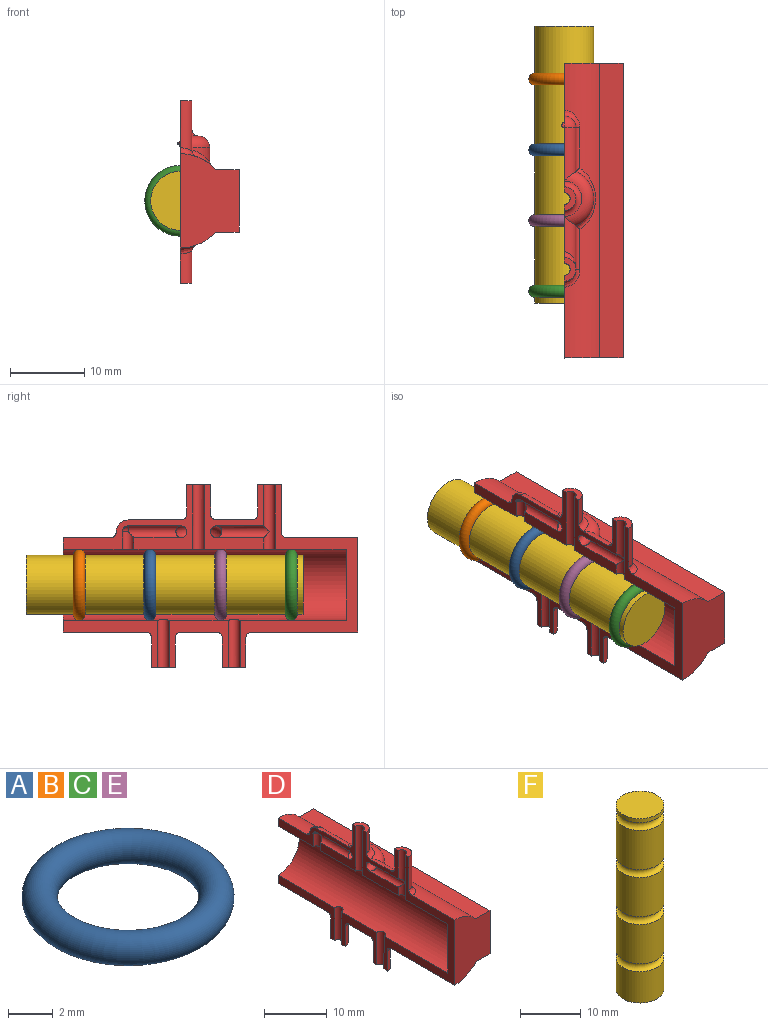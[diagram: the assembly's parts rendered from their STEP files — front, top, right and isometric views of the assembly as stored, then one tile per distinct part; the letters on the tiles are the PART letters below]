
ASSEMBLY  parts=6 mates=7
PART A: 1 faces, bbox 10.3x10.3x1.6 mm
  f0: torus R=3.97mm, axis (0,0,1), area 124.4mm2
PART B: same geometry as A
PART C: same geometry as A
PART D: 48 faces, bbox 11.2x41.4x26.3 mm
  f0: cylinder r=6.35mm len=39.69mm, axis (0,-1,0), area 153.3mm2, adj f29,f30,f31,f35,f36,f37,f38,f39
  f1: cylinder r=4.76mm len=38.1mm, axis (0,1,0), area 565.1mm2, adj f2,f3,f4,f5,f6,f22,f30,f31
  f2: cylinder r=0.79mm len=8.73mm, axis (0,0,1), area 20.8mm2, adj f1,f9,f15,f30,f34
  f3: cylinder r=0.79mm len=8.73mm, axis (0,0,1), area 21.8mm2, adj f1,f14,f31,f34
  f4: cylinder r=0.79mm len=2.38mm, axis (0,0,1), area 5.4mm2, adj f1,f11,f12,f31
  f5: cylinder r=0.79mm len=6.35mm, axis (0,0,-1), area 15.8mm2, adj f1,f28,f30,f33
  f6: cylinder r=0.79mm len=6.35mm, axis (0,0,-1), area 15.8mm2, adj f1,f27,f32,f33
  f7: cylinder r=1.59mm len=1.59mm, axis (0,0,-1), area 0.5mm2, adj f16,f23,f39
  f8: cylinder r=1.59mm len=6.76mm, axis (0,0,-1), area 28.4mm2, adj f15,f24,f30,f34,f35,f42
  f9: cylinder r=0.79mm len=7.14mm, axis (0,-1,0), area 16mm2, adj f2,f10,f34
  f10: torus R=2.38mm, axis (0,0,-1), area 35.4mm2, adj f9,f11,f31,f34
  f11: cylinder r=0.79mm len=7.14mm, axis (0,-1,0), area 16.5mm2, adj f4,f10,f12,f31
  f12: sphere r=0.79mm, area 1.3mm2, adj f4,f11,f31
  f13: cylinder r=1.59mm len=3.97mm, axis (0,0,-1), area 19.8mm2, adj f14,f31,f34,f43
  f14: plane 3.18x1.59mm, normal (0,0,1), area 3mm2, adj f3,f13,f31,f34
  f15: plane 3.18x1.59mm, normal (0,0,1), area 3mm2, adj f2,f8,f30,f34
  f16: sphere r=1.59mm, area 5.4mm2, adj f7,f17,f31
  f17: cylinder r=1.59mm len=7.14mm, axis (0,1,0), area 16.2mm2, adj f16,f23,f26,f31
  f18: cylinder r=1.59mm len=7.14mm, axis (0,-1,0), area 13.3mm2, adj f24,f26,f34,f42
  f19: cylinder r=1.59mm len=3.97mm, axis (0,0,1), area 19.8mm2, adj f27,f32,f33,f41
  f20: cylinder r=1.59mm len=3.97mm, axis (0,0,1), area 19.8mm2, adj f28,f30,f33,f40
  f21: cylinder r=6.35mm len=39.69mm, axis (0,-1,0), area 197.7mm2, adj f29,f30,f32,f33,f40,f41,f44,f46
  f22: plane 9.53x4.76mm, normal (0,1,0), area 35.6mm2, adj f1,f30
  f23: plane 5.89x0.41mm, normal (1,0,0), area 2.4mm2, adj f7,f17,f25,f37,f38
  f24: plane 5.89x0.41mm, normal (1,0,0), area 2.4mm2, adj f8,f18,f25,f36,f37
  f25: cylinder r=3.97mm len=7.28mm, axis (0,0,-1), area 10.6mm2, adj f23,f24,f26,f37
  f26: torus R=2.38mm, axis (0,0,1), area 22.8mm2, adj f17,f18,f25,f43
  f27: plane 3.18x1.59mm, normal (0,0,-1), area 3mm2, adj f6,f19,f32,f33
  f28: plane 3.18x1.59mm, normal (0,0,-1), area 3mm2, adj f5,f20,f30,f33
  f29: plane 12.7x7.94mm, normal (0,-1,0), area 80.9mm2, adj f0,f21,f30,f45,f46,f47
  f30: plane 24.63x15.9mm, normal (-1,0,0), area 67.7mm2, adj f0,f1,f2,f5,f8,f15,f20,f21
  f31: plane 19.16x10.43mm, normal (-1,0,0), area 39.8mm2, adj f0,f1,f3,f4,f10,f11,f12,f13
  f32: plane 12.73x6.38mm, normal (-1,0,0), area 24.1mm2, adj f1,f6,f19,f21,f27,f41,f44
  f33: plane 7.96x6.38mm, normal (-1,0,0), area 20.4mm2, adj f1,f5,f6,f19,f20,f21,f27,f28
  f34: plane 8.76x7.96mm, normal (-1,0,0), area 28.3mm2, adj f1,f2,f3,f8,f9,f10,f13,f14
  f35: bspline ~2.9x2.42mm, area 3.2mm2, adj f0,f8,f30,f36
  f36: cylinder r=0.79mm len=5.87mm, axis (0,-1,0), area 5.5mm2, adj f0,f24,f35,f37
  f37: bspline ~9.2x3.36mm, area 8.5mm2, adj f0,f23,f24,f25,f36,f38
  f38: cylinder r=0.79mm len=5.87mm, axis (0,-1,0), area 5.5mm2, adj f0,f23,f37,f39
  f39: bspline ~2.9x2.42mm, area 3.2mm2, adj f0,f7,f31,f38
  f40: bspline ~4.76x2.57mm, area 6.4mm2, adj f20,f21,f30,f33
  f41: bspline ~4.76x2.57mm, area 6.4mm2, adj f19,f21,f32,f33
  f42: bspline ~2.38x2.38mm, area 1.3mm2, adj f8,f18,f34
  f43: torus R=2.38mm, axis (0,0,1), area 7.3mm2, adj f13,f26,f31,f34
  f44: plane 12.7x7.94mm, normal (0,1,0), area 45.2mm2, adj f0,f1,f21,f31,f32,f45,f46,f47
  f45: plane 39.69x3.18mm, normal (0,0,1), area 126mm2, adj f0,f29,f44,f47
  f46: plane 39.69x3.18mm, normal (0,0,-1), area 126mm2, adj f21,f29,f44,f47
  f47: plane 39.69x8.4mm, normal (1,0,0), area 333.4mm2, adj f29,f44,f45,f46
PART E: same geometry as A
PART F: 11 faces, bbox 9.8x9.8x37.3 mm
  f0: cylinder r=3.97mm len=7.94mm, axis (0,0,-1), area 197.9mm2, adj f2,f3
  f1: cylinder r=3.97mm len=7.94mm, axis (0,0,-1), area 158.3mm2, adj f2,f10
  f2: torus R=3.97mm, axis (0,0,1), area 54.3mm2, adj f0,f1
  f3: torus R=3.97mm, axis (0,0,1), area 54.3mm2, adj f0,f4
  f4: cylinder r=3.97mm len=7.94mm, axis (0,0,-1), area 197.9mm2, adj f3,f5
  f5: torus R=3.97mm, axis (0,0,1), area 54.3mm2, adj f4,f6
  f6: cylinder r=3.97mm len=7.94mm, axis (0,0,-1), area 197.9mm2, adj f5,f7
  f7: torus R=3.97mm, axis (0,0,1), area 54.3mm2, adj f6,f8
  f8: cylinder r=3.97mm len=7.94mm, axis (0,0,-1), area 19.8mm2, adj f7,f9
  f9: plane 7.94x7.94mm, normal (0,0,1), area 49.5mm2, adj f8
  f10: plane 7.94x7.94mm, normal (0,0,-1), area 49.5mm2, adj f1
PLACE A rot(axis=(1,0,0),90deg) t=(-7.94,-10.88,4.2)mm
PLACE B rot(axis=(1,0,0),90deg) t=(-7.94,-1.35,4.2)mm
PLACE C rot(axis=(1,0,0),90deg) t=(-7.94,-29.93,4.2)mm
PLACE D rot(axis=(1,0,0),0deg) t=(-7.94,-6.35,4.2)mm
PLACE E rot(axis=(1,0,0),90deg) t=(-7.94,-20.4,4.2)mm
PLACE F rot(axis=(1,0.06,-0.06),90.2deg) t=(-7.94,5,4.2)mm
MATE cylindrical D.f1 <-> F.f0  axis (0,1,0) through (-7.94,-19.05,4.2)mm
MATE ball E.f0 <-> F.f0  axis (0,-1,0) through (-7.94,-21.19,4.2)mm
MATE cylindrical E.f0 <-> C.f0  axis (0,-1,0) through (-7.94,-21.19,4.2)mm
MATE ball F.f0 <-> C.f0  axis (0,-1,0) through (-7.94,-30.72,4.2)mm
MATE ball F.f0 <-> B.f0  axis (0,-1,0) through (-7.94,-2.14,4.2)mm
MATE ball F.f0 <-> A.f0  axis (0,-1,0) through (-7.94,-11.67,4.2)mm
MATE cylindrical B.f0 <-> A.f0  axis (0,-1,0) through (-7.94,-2.14,4.2)mm
